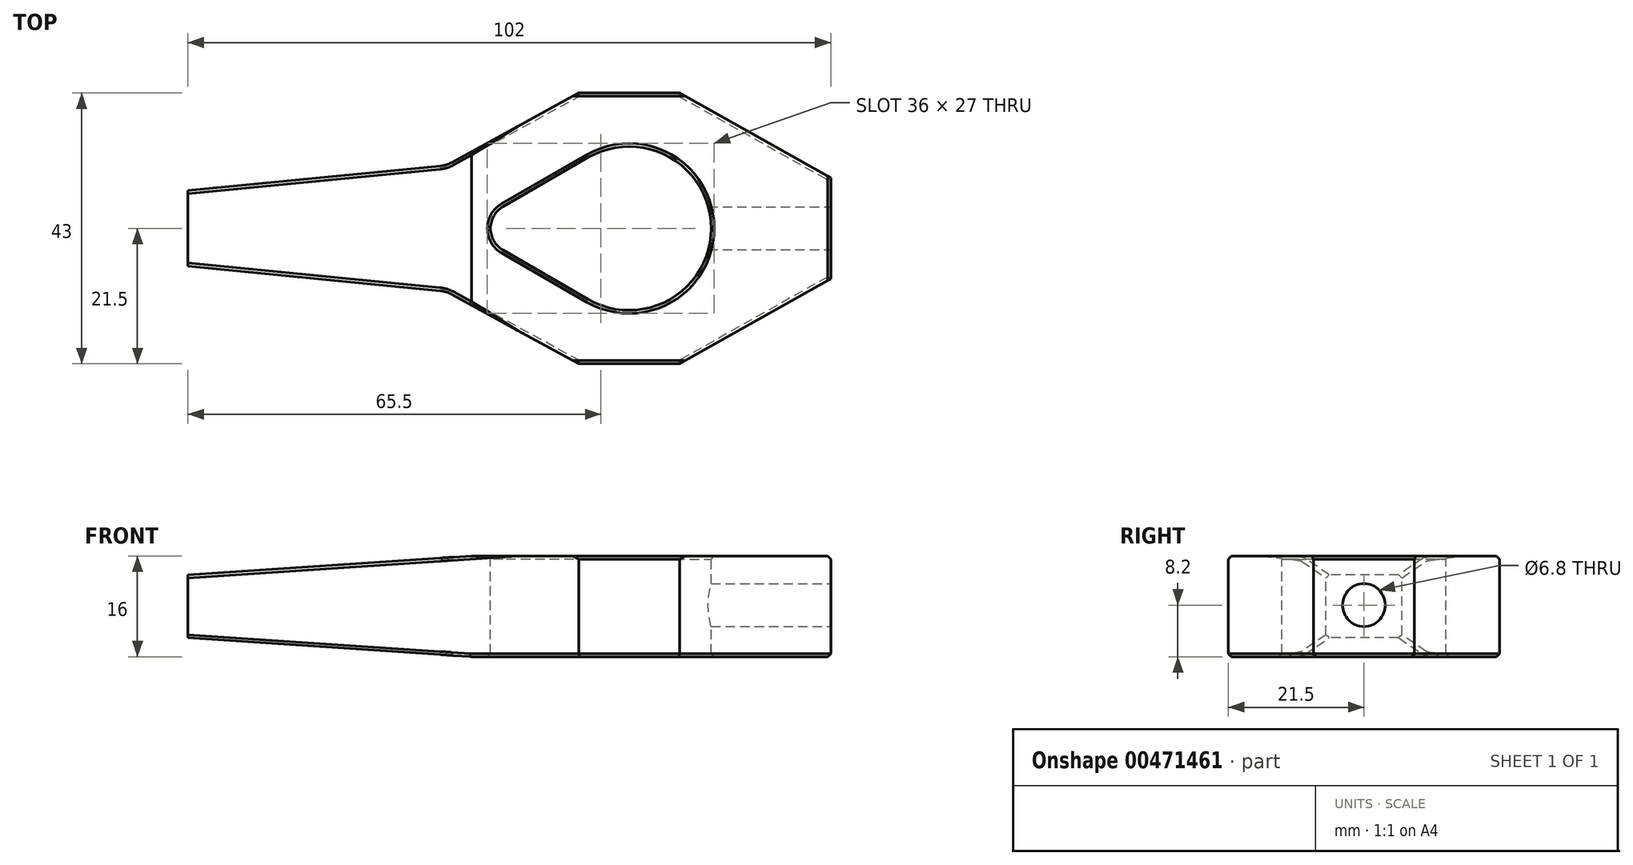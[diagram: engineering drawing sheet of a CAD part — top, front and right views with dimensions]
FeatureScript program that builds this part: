
annotation { "Feature Type Name" : "Feature", "Feature Type Description" : "" }
export const myFeature = defineFeature(function(context is Context, id is Id, definition is map)
    precondition{}
    {
        {
            var Q0;
            Q0=qCreatedBy(makeId("Top.planeOp"),FACE);
            var sketch = newSketch(context, id + "F0", { "sketchPlane" : qUnion([Q0])});
            skLineSegment(sketch, "E0.bottom", {"start": v(0, 0) * mm, "end": v(102, 0) * mm});
            skLineSegment(sketch, "E0.top", {"start": v(0, -43) * mm, "end": v(102, -43) * mm});
            skLineSegment(sketch, "E0.left", {"start": v(0, 0) * mm, "end": v(0, -43) * mm});
            skLineSegment(sketch, "E0.right", {"start": v(102, 0) * mm, "end": v(102, -43) * mm});
            skLineSegment(sketch, "E1", {"start": v(70, 5.97) * mm, "end": v(70, -48.97) * mm, "construction": true});
            skLineSegment(sketch, "E2", {"start": v(-8.42, -21.5) * mm, "end": v(112.42, -21.5) * mm, "construction": true});
            skPoint(sketch, "E2.startSnap0", {"position": v(0, -21.5) * mm});
            skArc(sketch, "E3", {"start": v(63.5, -32.76) * mm, "mid": v(83, -21.5) * mm, "end": v(63.5, -10.24) * mm});
            skLineSegment(sketch, "E4", {"start": v(52, 6.48) * mm, "end": v(52, -49.2) * mm, "construction": true});
            skPoint(sketch, "E4.startSnap0", {"position": v(52, -21.5) * mm});
            skArc(sketch, "E5", {"start": v(50, -18.04) * mm, "mid": v(48, -21.5) * mm, "end": v(50, -24.96) * mm});
            skLineSegment(sketch, "E6", {"start": v(63.5, -10.24) * mm, "end": v(50, -18.04) * mm});
            skLineSegment(sketch, "E7", {"start": v(50, -24.96) * mm, "end": v(63.5, -32.76) * mm});
            skSolve(sketch);
        }
        {
            var Q0;
            Q0=makeQuery(id+"F0.imprint","IMPRINT",FACE,{"disambiguationData":[TD([[makeQuery(id+"F0.imprint","IMPRINT",EDGE,{"derivedFrom":sQuery(id+"F0.wireOp",EDGE,"E0.bottom")}),-1.0]])]});
            extrude(context, id + "F1", {"entities" : qUnion([Q0]), "oppositeDirection" : true, "depth" : 16 * mm});
        }
        {
            var Q0;
            Q0=makeQuery(id+"F1.opExtrude","CAP_FACE",FACE,{"disambiguationData":[OSD([sQuery(id+"F0.wireOp",EDGE,"E0.bottom"),sQuery(id+"F0.wireOp",EDGE,"E0.top"),sQuery(id+"F0.wireOp",EDGE,"E0.left"),sQuery(id+"F0.wireOp",EDGE,"E0.right"),sQuery(id+"F0.wireOp",EDGE,"E3"),sQuery(id+"F0.wireOp",EDGE,"E5"),sQuery(id+"F0.wireOp",EDGE,"E6"),sQuery(id+"F0.wireOp",EDGE,"E7")])],"isStart":true});
            var sketch = newSketch(context, id + "F2", { "sketchPlane" : qUnion([Q0])});
            skPoint(sketch, "E8", {"position": v(62, -43) * mm});
            skPoint(sketch, "E9", {"position": v(78, -43) * mm});
            skPoint(sketch, "E10", {"position": v(0, -27.5) * mm});
            skPoint(sketch, "E11", {"position": v(0, -15.5) * mm});
            skPoint(sketch, "E12", {"position": v(62, 0) * mm});
            skPoint(sketch, "E13", {"position": v(78, 0) * mm});
            skPoint(sketch, "E14", {"position": v(102, -13.5) * mm});
            skPoint(sketch, "E15", {"position": v(102, -29.5) * mm});
            skPoint(sketch, "E16", {"position": v(41, 0) * mm});
            skLineSegment(sketch, "E17", {"start": v(0, -21.5) * mm, "end": v(102, -21.5) * mm, "construction": true});
            skLineSegment(sketch, "E18", {"start": v(70, -21.5) * mm, "end": v(70, -43) * mm, "construction": true});
            skLineSegment(sketch, "E19", {"start": v(70, -43) * mm, "end": v(70, -21.5) * mm, "construction": true});
            skLineSegment(sketch, "E20", {"start": v(70, 0) * mm, "end": v(70, -21.5) * mm, "construction": true});
            skLineSegment(sketch, "E21", {"start": v(41, 0) * mm, "end": v(41, -43) * mm, "construction": true});
            skPoint(sketch, "E22", {"position": v(41, -11.5) * mm});
            skPoint(sketch, "E23", {"position": v(41, -31.5) * mm});
            skLineSegment(sketch, "E24", {"start": v(0, -15.5) * mm, "end": v(41, -11.5) * mm});
            skLineSegment(sketch, "E25", {"start": v(62, 0) * mm, "end": v(41, -11.5) * mm});
            skLineSegment(sketch, "E26", {"start": v(78, 0) * mm, "end": v(62, 0) * mm});
            skLineSegment(sketch, "E27", {"start": v(78, 0) * mm, "end": v(102, -13.5) * mm});
            skLineSegment(sketch, "E28", {"start": v(102, -29.5) * mm, "end": v(102, -13.5) * mm});
            skLineSegment(sketch, "E29", {"start": v(102, -29.5) * mm, "end": v(78, -43) * mm});
            skLineSegment(sketch, "E30", {"start": v(62, -43) * mm, "end": v(78, -43) * mm});
            skLineSegment(sketch, "E31", {"start": v(62, -43) * mm, "end": v(41, -31.5) * mm});
            skLineSegment(sketch, "E32", {"start": v(41, -31.5) * mm, "end": v(0, -27.5) * mm});
            skLineSegment(sketch, "E33", {"start": v(0, -15.5) * mm, "end": v(0, -27.5) * mm});
            skSolve(sketch);
        }
        {
            var Q0;
            {var subQ0=sQuery(id+"F2.wireOp",EDGE,"E24");Q0=makeQuery(id+"F2.imprint","IMPRINT",FACE,{"disambiguationData":[TD([[makeQuery(id+"F2.imprint","IMPRINT",EDGE,{"derivedFrom":subQ0}),1.0]])]});}
            var Q1;
            {var subQ0=sQuery(id+"F2.wireOp",EDGE,"E27");Q1=makeQuery(id+"F2.imprint","IMPRINT",FACE,{"disambiguationData":[TD([[makeQuery(id+"F2.imprint","IMPRINT",EDGE,{"derivedFrom":subQ0}),1.0]])]});}
            var Q2;
            {var subQ0=sQuery(id+"F2.wireOp",EDGE,"E29");Q2=makeQuery(id+"F2.imprint","IMPRINT",FACE,{"disambiguationData":[TD([[makeQuery(id+"F2.imprint","IMPRINT",EDGE,{"derivedFrom":subQ0}),1.0]])]});}
            var Q3;
            {var subQ0=sQuery(id+"F2.wireOp",EDGE,"E31");Q3=makeQuery(id+"F2.imprint","IMPRINT",FACE,{"disambiguationData":[TD([[makeQuery(id+"F2.imprint","IMPRINT",EDGE,{"derivedFrom":subQ0}),1.0]])]});}
            extrude(context, id + "F3", {"entities" : qUnion([Q0, Q1, Q2, Q3]), "operationType" : NewBodyOperationType.REMOVE, "oppositeDirection" : true, "depth" : 40.8 * mm, "offsetDistance" : 25 * mm});
        }
        {
            var Q0;
            Q0=makeQuery(id+"F3.boolean.opBoolean","COPY",EDGE,{"derivedFrom":makeQuery(id+"F3.opExtrude","SWEPT_EDGE",EDGE,{"disambiguationData":[OSD([sQuery(id+"F2.wireOp",EDGE,"E24"),sQuery(id+"F2.wireOp",EDGE,"E25")])]})});
            var Q1;
            Q1=makeQuery(id+"F3.boolean.opBoolean","COPY",EDGE,{"derivedFrom":makeQuery(id+"F3.opExtrude","SWEPT_EDGE",EDGE,{"disambiguationData":[OSD([sQuery(id+"F2.wireOp",EDGE,"E31"),sQuery(id+"F2.wireOp",EDGE,"E32")])]})});
            fillet(context, id + "F4", {"entities" : qUnion([Q0, Q1]), "radius" : 5 * mm, "tangentPropagation" : true, "allowEdgeOverflow" : false});
        }
        {
            var Q0;
            Q0=makeQuery(id+"F1.opExtrude","SWEPT_FACE",FACE,{"disambiguationData":[OSD([sQuery(id+"F0.wireOp",EDGE,"E0.right")])]});
            var sketch = newSketch(context, id + "F5", { "sketchPlane" : qUnion([Q0])});
            skCircle(sketch, "E34", {"center": v(-21.5, -7.8) * mm, "radius": 3.4 * mm});
            skPoint(sketch, "E34.centerSnap0", {"position": v(-21.5, 0) * mm});
            skSolve(sketch);
        }
        {
            var Q0;
            Q0=makeQuery(id+"F5.imprint","IMPRINT",FACE,{"disambiguationData":[TD([[makeQuery(id+"F5.imprint","IMPRINT",EDGE,{"derivedFrom":sQuery(id+"F5.wireOp",EDGE,"E34")}),1.0]])]});
            extrude(context, id + "F6", {"entities" : qUnion([Q0]), "operationType" : NewBodyOperationType.REMOVE, "oppositeDirection" : true, "depth" : 25 * mm, "offsetDistance" : 25 * mm});
        }
        {
            var Q0;
            Q0=makeQuery(id+"F1.opExtrude","SWEPT_FACE",FACE,{"disambiguationData":[OSD([sQuery(id+"F0.wireOp",EDGE,"E0.top")])]});
            var sketch = newSketch(context, id + "F7", { "sketchPlane" : qUnion([Q0])});
            skPoint(sketch, "E35", {"position": v(45, 0) * mm});
            skPoint(sketch, "E36", {"position": v(0, -3) * mm});
            skPoint(sketch, "E37", {"position": v(0, -13) * mm});
            skPoint(sketch, "E38", {"position": v(0, -16) * mm});
            skPoint(sketch, "E39", {"position": v(45, -16) * mm});
            skLineSegment(sketch, "E40", {"start": v(0, -3) * mm, "end": v(45, 0) * mm});
            skLineSegment(sketch, "E41", {"start": v(0, 0) * mm, "end": v(45, 0) * mm});
            skLineSegment(sketch, "E42", {"start": v(0, 0) * mm, "end": v(0, -3) * mm});
            skLineSegment(sketch, "E43", {"start": v(0, -13) * mm, "end": v(0, -16) * mm});
            skLineSegment(sketch, "E44", {"start": v(45, -16) * mm, "end": v(0, -16) * mm});
            skLineSegment(sketch, "E45", {"start": v(0, -13) * mm, "end": v(45, -16) * mm});
            skSolve(sketch);
        }
        {
            var Q0;
            Q0 = qSketchRegion(id + "F7", true);
            extrude(context, id + "F8", {"entities" : qUnion([Q0]), "operationType" : NewBodyOperationType.REMOVE, "oppositeDirection" : true, "depth" : 66.7 * mm, "offsetDistance" : 25 * mm});
        }
        {
            var Q0;
            Q0=makeQuery(id+"F1.opExtrude","CAP_EDGE",EDGE,{"disambiguationData":[OSD([sQuery(id+"F0.wireOp",EDGE,"E0.top")])],"isStart":true});
            var Q1;
            Q1=makeQuery(id+"F3.boolean.opBoolean","COPY",EDGE,{"derivedFrom":makeQuery(id+"F3.opExtrude","CAP_EDGE",EDGE,{"disambiguationData":[OSD([sQuery(id+"F2.wireOp",EDGE,"E29")])],"isStart":true})});
            var Q2;
            Q2=makeQuery(id+"F3.boolean.opBoolean","COPY",EDGE,{"derivedFrom":makeQuery(id+"F3.opExtrude","CAP_EDGE",EDGE,{"disambiguationData":[OSD([sQuery(id+"F2.wireOp",EDGE,"E31")])],"isStart":true})});
            var Q3;
            Q3=makeQuery(id+"F1.opExtrude","CAP_EDGE",EDGE,{"disambiguationData":[OSD([sQuery(id+"F0.wireOp",EDGE,"E0.right")])],"isStart":true});
            var Q4;
            Q4=makeQuery(id+"F3.boolean.opBoolean","COPY",EDGE,{"derivedFrom":makeQuery(id+"F3.opExtrude","CAP_EDGE",EDGE,{"disambiguationData":[OSD([sQuery(id+"F2.wireOp",EDGE,"E27")])],"isStart":true})});
            var Q5;
            Q5=makeQuery(id+"F1.opExtrude","CAP_EDGE",EDGE,{"disambiguationData":[OSD([sQuery(id+"F0.wireOp",EDGE,"E0.bottom")])],"isStart":true});
            var Q6;
            Q6=makeQuery(id+"F3.boolean.opBoolean","COPY",EDGE,{"derivedFrom":makeQuery(id+"F3.opExtrude","CAP_EDGE",EDGE,{"disambiguationData":[OSD([sQuery(id+"F2.wireOp",EDGE,"E25")])],"isStart":true})});
            var Q7;
            Q7=makeQuery(id+"F1.opExtrude","CAP_EDGE",EDGE,{"disambiguationData":[OSD([sQuery(id+"F0.wireOp",EDGE,"E3")])],"isStart":true});
            var Q8;
            Q8=makeQuery(id+"F1.opExtrude","CAP_EDGE",EDGE,{"disambiguationData":[OSD([sQuery(id+"F0.wireOp",EDGE,"E6")])],"isStart":true});
            var Q9;
            Q9=makeQuery(id+"F1.opExtrude","CAP_EDGE",EDGE,{"disambiguationData":[OSD([sQuery(id+"F0.wireOp",EDGE,"E0.right")])],"isStart":false});
            var Q10;
            Q10=makeQuery(id+"F3.boolean.opBoolean","INTERSECT",EDGE,{"derivedFrom":[makeQuery(id+"F1.opExtrude","CAP_FACE",FACE,{"disambiguationData":[OSD([sQuery(id+"F0.wireOp",EDGE,"E0.bottom"),sQuery(id+"F0.wireOp",EDGE,"E0.top"),sQuery(id+"F0.wireOp",EDGE,"E0.left"),sQuery(id+"F0.wireOp",EDGE,"E0.right"),sQuery(id+"F0.wireOp",EDGE,"E3"),sQuery(id+"F0.wireOp",EDGE,"E5"),sQuery(id+"F0.wireOp",EDGE,"E6"),sQuery(id+"F0.wireOp",EDGE,"E7")])],"isStart":false}),makeQuery(id+"F3.opExtrude","SWEPT_FACE",FACE,{"disambiguationData":[OSD([sQuery(id+"F2.wireOp",EDGE,"E27")])]})]});
            var Q11;
            Q11=makeQuery(id+"F1.opExtrude","CAP_EDGE",EDGE,{"disambiguationData":[OSD([sQuery(id+"F0.wireOp",EDGE,"E0.bottom")])],"isStart":false});
            var Q12;
            Q12=makeQuery(id+"F3.boolean.opBoolean","INTERSECT",EDGE,{"derivedFrom":[makeQuery(id+"F1.opExtrude","CAP_FACE",FACE,{"disambiguationData":[OSD([sQuery(id+"F0.wireOp",EDGE,"E0.bottom"),sQuery(id+"F0.wireOp",EDGE,"E0.top"),sQuery(id+"F0.wireOp",EDGE,"E0.left"),sQuery(id+"F0.wireOp",EDGE,"E0.right"),sQuery(id+"F0.wireOp",EDGE,"E3"),sQuery(id+"F0.wireOp",EDGE,"E5"),sQuery(id+"F0.wireOp",EDGE,"E6"),sQuery(id+"F0.wireOp",EDGE,"E7")])],"isStart":false}),makeQuery(id+"F3.opExtrude","SWEPT_FACE",FACE,{"disambiguationData":[OSD([sQuery(id+"F2.wireOp",EDGE,"E25")])]})]});
            var Q13;
            Q13=makeQuery(id+"F3.boolean.opBoolean","INTERSECT",EDGE,{"derivedFrom":[makeQuery(id+"F1.opExtrude","CAP_FACE",FACE,{"disambiguationData":[OSD([sQuery(id+"F0.wireOp",EDGE,"E0.bottom"),sQuery(id+"F0.wireOp",EDGE,"E0.top"),sQuery(id+"F0.wireOp",EDGE,"E0.left"),sQuery(id+"F0.wireOp",EDGE,"E0.right"),sQuery(id+"F0.wireOp",EDGE,"E3"),sQuery(id+"F0.wireOp",EDGE,"E5"),sQuery(id+"F0.wireOp",EDGE,"E6"),sQuery(id+"F0.wireOp",EDGE,"E7")])],"isStart":false}),makeQuery(id+"F3.opExtrude","SWEPT_FACE",FACE,{"disambiguationData":[OSD([sQuery(id+"F2.wireOp",EDGE,"E31")])]})]});
            var Q14;
            Q14=makeQuery(id+"F1.opExtrude","CAP_EDGE",EDGE,{"disambiguationData":[OSD([sQuery(id+"F0.wireOp",EDGE,"E0.top")])],"isStart":false});
            var Q15;
            Q15=makeQuery(id+"F3.boolean.opBoolean","INTERSECT",EDGE,{"derivedFrom":[makeQuery(id+"F1.opExtrude","CAP_FACE",FACE,{"disambiguationData":[OSD([sQuery(id+"F0.wireOp",EDGE,"E0.bottom"),sQuery(id+"F0.wireOp",EDGE,"E0.top"),sQuery(id+"F0.wireOp",EDGE,"E0.left"),sQuery(id+"F0.wireOp",EDGE,"E0.right"),sQuery(id+"F0.wireOp",EDGE,"E3"),sQuery(id+"F0.wireOp",EDGE,"E5"),sQuery(id+"F0.wireOp",EDGE,"E6"),sQuery(id+"F0.wireOp",EDGE,"E7")])],"isStart":false}),makeQuery(id+"F3.opExtrude","SWEPT_FACE",FACE,{"disambiguationData":[OSD([sQuery(id+"F2.wireOp",EDGE,"E29")])]})]});
            var Q16;
            Q16=makeQuery(id+"F1.opExtrude","CAP_EDGE",EDGE,{"disambiguationData":[OSD([sQuery(id+"F0.wireOp",EDGE,"E3")])],"isStart":false});
            var Q17;
            Q17=makeQuery(id+"F1.opExtrude","CAP_EDGE",EDGE,{"disambiguationData":[OSD([sQuery(id+"F0.wireOp",EDGE,"E7")])],"isStart":false});
            var Q18;
            Q18=makeQuery(id+"F8.boolean.opBoolean","INTERSECT",EDGE,{"derivedFrom":[makeQuery(id+"F3.boolean.opBoolean","COPY",FACE,{"derivedFrom":makeQuery(id+"F3.opExtrude","SWEPT_FACE",FACE,{"disambiguationData":[OSD([sQuery(id+"F2.wireOp",EDGE,"E24")])]})}),makeQuery(id+"F8.opExtrude","SWEPT_FACE",FACE,{"disambiguationData":[OSD([sQuery(id+"F7.wireOp",EDGE,"E40")])]})]});
            var Q19;
            Q19=makeQuery(id+"F8.boolean.opBoolean","INTERSECT",EDGE,{"derivedFrom":[makeQuery(id+"F3.boolean.opBoolean","COPY",FACE,{"derivedFrom":makeQuery(id+"F3.opExtrude","SWEPT_FACE",FACE,{"disambiguationData":[OSD([sQuery(id+"F2.wireOp",EDGE,"E32")])]})}),makeQuery(id+"F8.opExtrude","SWEPT_FACE",FACE,{"disambiguationData":[OSD([sQuery(id+"F7.wireOp",EDGE,"E40")])]})]});
            var Q20;
            Q20=makeQuery(id+"F8.boolean.opBoolean","INTERSECT",EDGE,{"derivedFrom":[makeQuery(id+"F3.boolean.opBoolean","COPY",FACE,{"derivedFrom":makeQuery(id+"F3.opExtrude","SWEPT_FACE",FACE,{"disambiguationData":[OSD([sQuery(id+"F2.wireOp",EDGE,"E32")])]})}),makeQuery(id+"F8.opExtrude","SWEPT_FACE",FACE,{"disambiguationData":[OSD([sQuery(id+"F7.wireOp",EDGE,"E45")])]})]});
            var Q21;
            Q21=makeQuery(id+"F8.boolean.opBoolean","INTERSECT",EDGE,{"derivedFrom":[makeQuery(id+"F3.boolean.opBoolean","COPY",FACE,{"derivedFrom":makeQuery(id+"F3.opExtrude","SWEPT_FACE",FACE,{"disambiguationData":[OSD([sQuery(id+"F2.wireOp",EDGE,"E24")])]})}),makeQuery(id+"F8.opExtrude","SWEPT_FACE",FACE,{"disambiguationData":[OSD([sQuery(id+"F7.wireOp",EDGE,"E45")])]})]});
            chamfer(context, id + "F9", {"entities" : qUnion([Q0, Q1, Q2, Q3, Q4, Q5, Q6, Q7, Q8, Q9, Q10, Q11, Q12, Q13, Q14, Q15, Q16, Q17, Q18, Q19, Q20, Q21]), "width" : .5 * mm, "tangentPropagation" : true});
        }
    });
